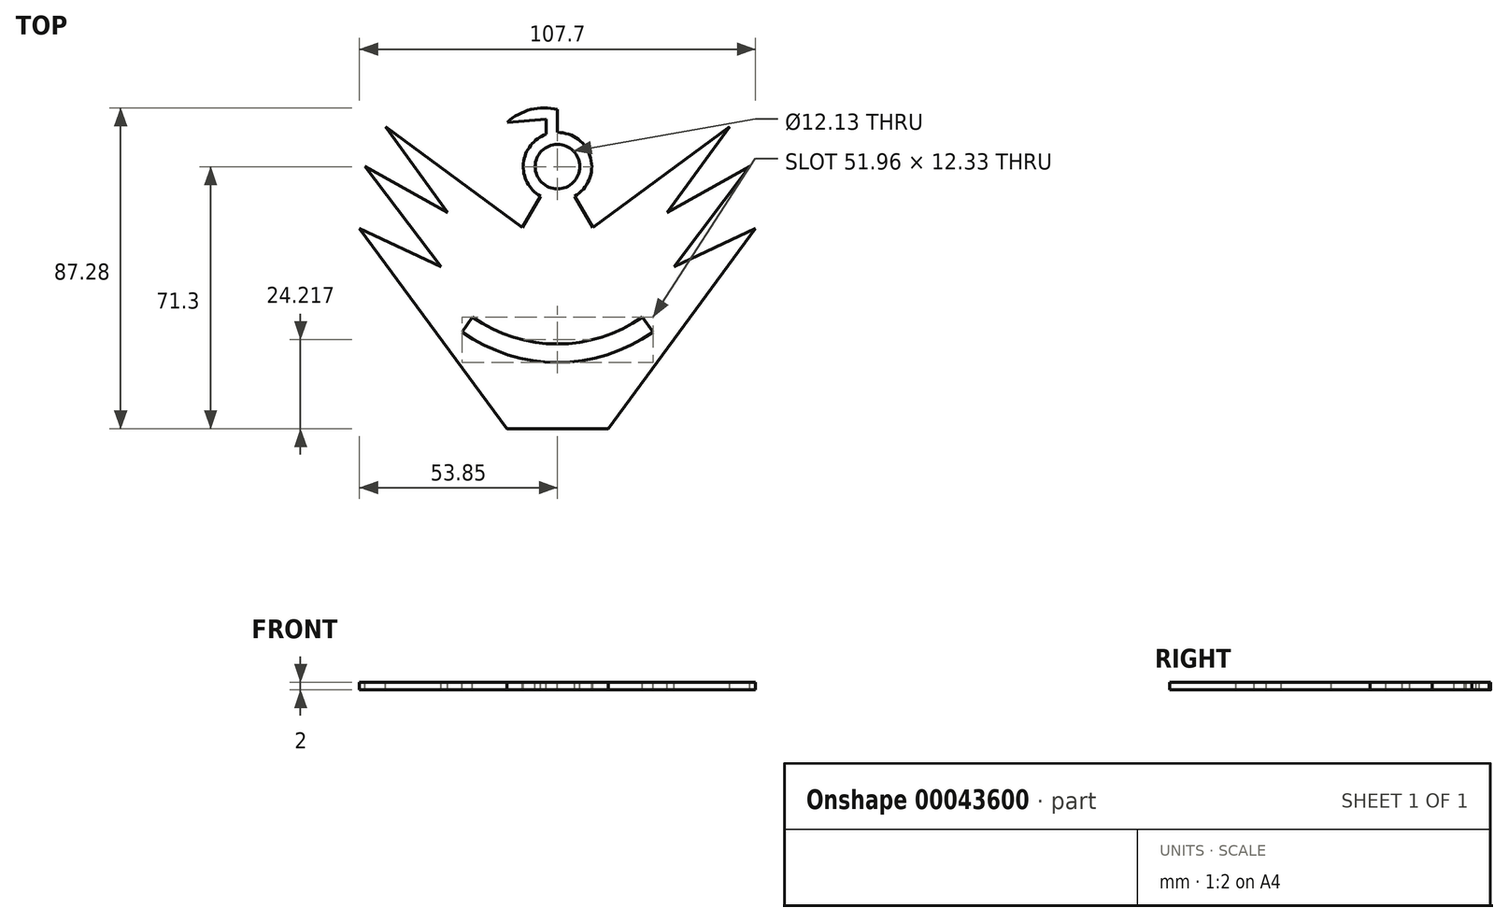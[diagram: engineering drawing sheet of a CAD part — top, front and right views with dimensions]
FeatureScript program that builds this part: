
annotation { "Feature Type Name" : "Feature", "Feature Type Description" : "" }
export const myFeature = defineFeature(function(context is Context, id is Id, definition is map)
    precondition{}
    {
        {
            var Q0;
            Q0=qCreatedBy(makeId("Top.planeOp"),FACE);
            var sketch = newSketch(context, id + "F0", { "sketchPlane" : qUnion([Q0])});
            skPoint(sketch, "E0.0.midPoint", {"position": v(0, 15) * mm});
            skLineSegment(sketch, "E1.MirrorCS", {"start": v(-4.65, 51.94) * mm, "end": v(-9.56, 43.44) * mm});
            skLineSegment(sketch, "E2.MirrorCS", {"start": v(9.56, 43.44) * mm, "end": v(4.65, 51.94) * mm});
            skCircle(sketch, "E3", {"center": v(0, 60) * mm, "radius": 9.3 * mm});
            skLineSegment(sketch, "E4", {"start": v(-9.56, 43.44) * mm, "end": v(-46.77, 70.86) * mm});
            skLineSegment(sketch, "E5", {"start": v(-46.77, 70.86) * mm, "end": v(-29.85, 47.48) * mm});
            skLineSegment(sketch, "E6", {"start": v(-29.85, 47.48) * mm, "end": v(-52.31, 60.1) * mm});
            skLineSegment(sketch, "E7", {"start": v(-52.31, 60.1) * mm, "end": v(-31.7, 32.71) * mm});
            skLineSegment(sketch, "E8", {"start": v(-31.7, 32.71) * mm, "end": v(-53.85, 43.17) * mm});
            skLineSegment(sketch, "E9", {"start": v(-53.85, 43.17) * mm, "end": v(-13.76, -11.3) * mm});
            skLineSegment(sketch, "E10", {"start": v(0, 51.78) * mm, "end": v(0, 50.7) * mm});
            skLineSegment(sketch, "E11.MirrorCS", {"start": v(9.56, 43.44) * mm, "end": v(46.77, 70.86) * mm});
            skLineSegment(sketch, "E12.MirrorCS", {"start": v(46.77, 70.86) * mm, "end": v(29.85, 47.48) * mm});
            skLineSegment(sketch, "E13.MirrorCS", {"start": v(29.85, 47.48) * mm, "end": v(52.31, 60.1) * mm});
            skLineSegment(sketch, "E14.MirrorCS", {"start": v(52.31, 60.1) * mm, "end": v(31.7, 32.71) * mm});
            skLineSegment(sketch, "E15.MirrorCS", {"start": v(31.7, 32.71) * mm, "end": v(53.85, 43.17) * mm});
            skLineSegment(sketch, "E16.MirrorCS", {"start": v(53.85, 43.17) * mm, "end": v(13.76, -11.3) * mm});
            skArc(sketch, "E17", {"start": v(0, 75.54) * mm, "mid": v(-7.26, 75.51) * mm, "end": v(-13.63, 72.05) * mm});
            skArc(sketch, "E18.MirrorCS", {"start": v(0, 75.54) * mm, "mid": v(7.26, 75.51) * mm, "end": v(13.63, 72.05) * mm});
            skArc(sketch, "E19", {"start": v(-25.98, 15) * mm, "mid": v(0, 6.75) * mm, "end": v(25.98, 15) * mm});
            skArc(sketch, "E20.0", {"start": v(-23.1, 19.08) * mm, "mid": v(0, 11.75) * mm, "end": v(23.1, 19.08) * mm});
            skPoint(sketch, "E21.orphan", {"position": v(-25.98, 15) * mm});
            skLineSegment(sketch, "E22", {"start": v(-3.06, 68.79) * mm, "end": v(-3.06, 72.89) * mm});
            skLineSegment(sketch, "E23", {"start": v(-3.06, 72.89) * mm, "end": v(-13.63, 72.05) * mm});
            skLineSegment(sketch, "E24", {"start": v(0, 75.54) * mm, "end": v(0, 69.3) * mm});
            skLineSegment(sketch, "E25.MirrorCS", {"start": v(3.06, 72.89) * mm, "end": v(13.63, 72.05) * mm});
            skLineSegment(sketch, "E26.MirrorCS", {"start": v(3.06, 68.79) * mm, "end": v(3.06, 72.89) * mm});
            skPoint(sketch, "E27.orphan", {"position": v(0, 70.97) * mm});
            skPoint(sketch, "E28.start.orphan", {"position": v(-7.26, 75.51) * mm});
            skPoint(sketch, "E29.end.orphan", {"position": v(7.26, 75.51) * mm});
            skPoint(sketch, "E30.orphan", {"position": v(25.98, 15) * mm});
            skPoint(sketch, "E31.MirrorC.center.orphan", {"position": v(0, 30) * mm});
            skLineSegment(sketch, "E32", {"start": v(-25.98, 15) * mm, "end": v(-23.1, 19.08) * mm});
            skLineSegment(sketch, "E33", {"start": v(23.1, 19.08) * mm, "end": v(25.98, 15) * mm});
            skPoint(sketch, "E0.cCircle.center.orphan", {"position": v(0, 0) * mm});
            skLineSegment(sketch, "E34", {"start": v(-13.76, -11.3) * mm, "end": v(13.76, -11.3) * mm});
            skPoint(sketch, "E35.orphan", {"position": v(0, -30) * mm});
            skCircle(sketch, "E36.0", {"center": v(0, 60) * mm, "radius": 6.07 * mm});
            skSolve(sketch);
        }
        {
            var Q0;
            {var subQ3=sQuery(id+"F0.wireOp",EDGE,"E1.MirrorCS");Q0=makeQuery(id+"F0.imprint","IMPRINT",FACE,{"disambiguationData":[TD([[makeQuery(id+"F0.imprint","IMPRINT",EDGE,{"derivedFrom":subQ3}),1.0]])]});}
            var Q1;
            Q1=makeQuery(id+"F0.imprint","IMPRINT",FACE,{"disambiguationData":[TD([[makeQuery(id+"F0.imprint","IMPRINT",EDGE,{"derivedFrom":sQuery(id+"F0.wireOp",EDGE,"E36.0")}),-1.0]])]});
            var Q2;
            Q2=makeQuery(id+"F0.imprint","IMPRINT",FACE,{"disambiguationData":[TD([[makeQuery(id+"F0.imprint","IMPRINT",EDGE,{"derivedFrom":sQuery(id+"F0.wireOp",EDGE,"E18.MirrorCS")}),-1.0]])]});
            var Q3;
            Q3=makeQuery(id+"F0.imprint","IMPRINT",FACE,{"disambiguationData":[TD([[makeQuery(id+"F0.imprint","IMPRINT",EDGE,{"derivedFrom":sQuery(id+"F0.wireOp",EDGE,"E17")}),1.0]])]});
            extrude(context, id + "F1", {"entities" : qUnion([Q0, Q1, Q2, Q3]), "oppositeDirection" : true, "depth" : 2 * mm});
        }
    });
